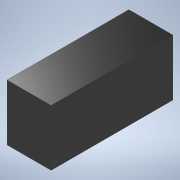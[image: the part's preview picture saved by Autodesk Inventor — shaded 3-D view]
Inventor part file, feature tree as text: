
AUTODESK INVENTOR PART (.ipt)
format: ipt  version: 2020 (Build 240168000, 168)  size: 89,088 bytes
history: native  units: mm
features: other x1, extrude x1, sketch x1
ambient origin geometry x8: Origin, YZ Plane, XZ Plane, XY Plane, X Axis, Y Axis, Z Axis, Center Point
bodies: Body1 (feature_tree)
feature tree (3):
  other  "솔리드1"
  extrude  "돌출1"  Depth=4.7mm
  sketch  "스케치1"
